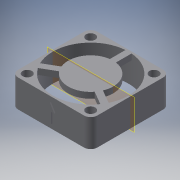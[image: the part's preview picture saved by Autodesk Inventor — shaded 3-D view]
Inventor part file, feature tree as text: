
AUTODESK INVENTOR PART (.ipt)
format: ipt  version: 2018 (Build 220112000, 112)  size: 129,024 bytes
history: native  units: mm
features: plane x1, other x1
ambient origin geometry x8: Origin, YZ Plane, XZ Plane, XY Plane, X Axis, Y Axis, Z Axis, Center Point
bodies: Solid1 (feature_tree)
feature tree (2):
  plane  "Work Plane1"
  other  "Part 1"
